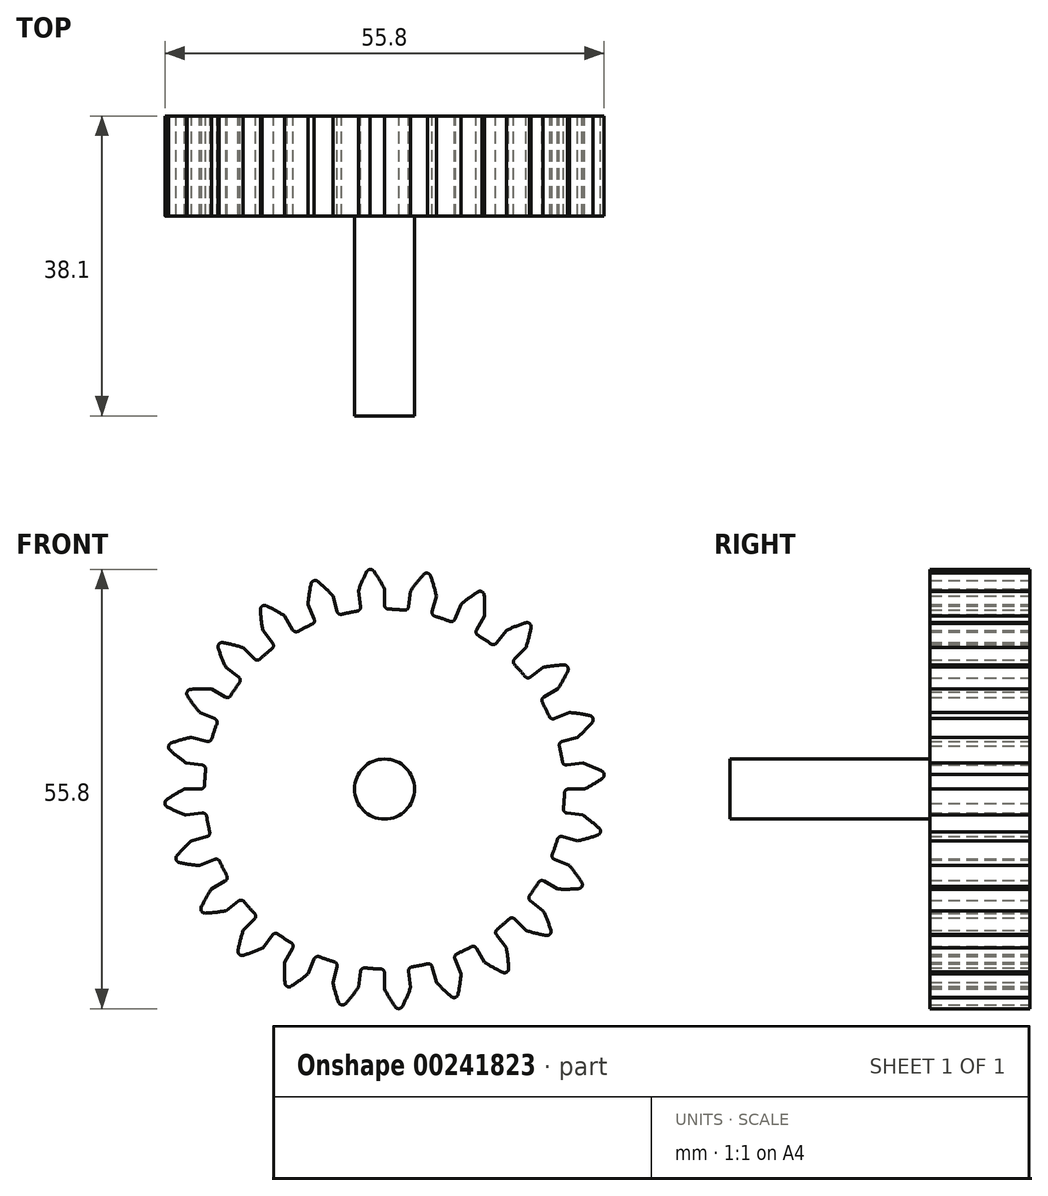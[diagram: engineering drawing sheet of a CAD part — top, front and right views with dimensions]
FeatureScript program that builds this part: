
annotation { "Feature Type Name" : "Feature", "Feature Type Description" : "" }
export const myFeature = defineFeature(function(context is Context, id is Id, definition is map)
    precondition{}
    {
        {
            var Q0;
            Q0=qCreatedBy(makeId("Front.planeOp"),FACE);
            var sketch = newSketch(context, id + "F0", { "sketchPlane" : qUnion([Q0])});
            skArc(sketch, "E0", {"start": v(-3.48, 22.6) * mm, "mid": v(1.5, -22.81) * mm, "end": v(0.5, 22.85) * mm});
            skLineSegment(sketch, "E1", {"start": v(0, 0) * mm, "end": v(-3.07, 46.82) * mm, "construction": true});
            skArc(sketch, "E2", {"start": v(0, 25.4) * mm, "mid": v(-0.64, 26.56) * mm, "end": v(-1.37, 27.68) * mm});
            skLineSegment(sketch, "E3", {"start": v(-1.78, 27.9) * mm, "end": v(-1.83, 27.9) * mm});
            skLineSegment(sketch, "E4", {"start": v(0, 25.4) * mm, "end": v(0, 23.36) * mm});
            skLineSegment(sketch, "E5.MirrorCS", {"start": v(-1.87, 27.9) * mm, "end": v(-1.83, 27.9) * mm});
            skArc(sketch, "E6.MirrorCS", {"start": v(-3.32, 25.18) * mm, "mid": v(-2.83, 26.42) * mm, "end": v(-2.26, 27.62) * mm});
            skLineSegment(sketch, "E7.MirrorCS", {"start": v(-3.32, 25.18) * mm, "end": v(-3.05, 23.16) * mm});
            skPoint(sketch, "E8.visualSharp", {"position": v(-2.13, 27.86) * mm});
            skArc(sketch, "E8.filletArc", {"start": v(-1.87, 27.9) * mm, "mid": v(-2.1, 27.8) * mm, "end": v(-2.26, 27.62) * mm});
            skPoint(sketch, "E9.visualSharp", {"position": v(0, 22.86) * mm});
            skArc(sketch, "E9.filletArc", {"start": v(0, 23.36) * mm, "mid": v(0.14, 23) * mm, "end": v(0.5, 22.85) * mm});
            skPoint(sketch, "E10.visualSharp", {"position": v(-1.52, 27.9) * mm});
            skArc(sketch, "E10.filletArc", {"start": v(-1.37, 27.68) * mm, "mid": v(-1.55, 27.84) * mm, "end": v(-1.78, 27.9) * mm});
            skPoint(sketch, "E11.visualSharp", {"position": v(-2.98, 22.66) * mm});
            skArc(sketch, "E11.filletArc", {"start": v(-3.48, 22.6) * mm, "mid": v(-3.15, 22.8) * mm, "end": v(-3.05, 23.16) * mm});
            skArc(sketch, "E12.1.0", {"start": v(-9.03, 26.46) * mm, "mid": v(-9.22, 26.31) * mm, "end": v(-9.33, 26.1) * mm});
            skLineSegment(sketch, "E12.1.1", {"start": v(-9.03, 26.46) * mm, "end": v(-8.99, 26.47) * mm});
            skLineSegment(sketch, "E12.1.2", {"start": v(-8.94, 26.49) * mm, "end": v(-8.99, 26.47) * mm});
            skArc(sketch, "E12.1.3", {"start": v(-8.49, 26.38) * mm, "mid": v(-8.7, 26.5) * mm, "end": v(-8.94, 26.49) * mm});
            skArc(sketch, "E12.1.4", {"start": v(-6.57, 24.53) * mm, "mid": v(-7.5, 25.5) * mm, "end": v(-8.49, 26.38) * mm});
            skArc(sketch, "E12.1.5", {"start": v(-9.72, 23.47) * mm, "mid": v(-9.57, 24.79) * mm, "end": v(-9.33, 26.1) * mm});
            skLineSegment(sketch, "E12.1.6", {"start": v(-6.57, 24.53) * mm, "end": v(-6.05, 22.57) * mm});
            skArc(sketch, "E12.1.7", {"start": v(-6.05, 22.57) * mm, "mid": v(-5.81, 22.26) * mm, "end": v(-5.44, 22.2) * mm});
            skArc(sketch, "E12.1.8", {"start": v(-9.2, 20.92) * mm, "mid": v(-8.94, 21.2) * mm, "end": v(-8.94, 21.58) * mm});
            skLineSegment(sketch, "E12.1.9", {"start": v(-9.72, 23.47) * mm, "end": v(-8.94, 21.58) * mm});
            skArc(sketch, "E12.2.0", {"start": v(-15.57, 23.22) * mm, "mid": v(-15.72, 23.03) * mm, "end": v(-15.77, 22.8) * mm});
            skLineSegment(sketch, "E12.2.1", {"start": v(-15.57, 23.22) * mm, "end": v(-15.53, 23.25) * mm});
            skLineSegment(sketch, "E12.2.2", {"start": v(-15.5, 23.27) * mm, "end": v(-15.53, 23.25) * mm});
            skArc(sketch, "E12.2.3", {"start": v(-15.03, 23.29) * mm, "mid": v(-15.26, 23.34) * mm, "end": v(-15.5, 23.27) * mm});
            skArc(sketch, "E12.2.4", {"start": v(-12.7, 22) * mm, "mid": v(-13.84, 22.68) * mm, "end": v(-15.03, 23.29) * mm});
            skArc(sketch, "E12.2.5", {"start": v(-15.46, 20.15) * mm, "mid": v(-15.66, 21.47) * mm, "end": v(-15.77, 22.8) * mm});
            skLineSegment(sketch, "E12.2.6", {"start": v(-12.7, 22) * mm, "end": v(-11.68, 20.23) * mm});
            skArc(sketch, "E12.2.7", {"start": v(-11.68, 20.23) * mm, "mid": v(-11.38, 20) * mm, "end": v(-11, 20.04) * mm});
            skArc(sketch, "E12.2.8", {"start": v(-14.3, 17.83) * mm, "mid": v(-14.12, 18.16) * mm, "end": v(-14.22, 18.53) * mm});
            skLineSegment(sketch, "E12.2.9", {"start": v(-15.46, 20.15) * mm, "end": v(-14.22, 18.53) * mm});
            skArc(sketch, "E12.3.0", {"start": v(-21.05, 18.4) * mm, "mid": v(-21.14, 18.18) * mm, "end": v(-21.13, 17.94) * mm});
            skLineSegment(sketch, "E12.3.1", {"start": v(-21.05, 18.4) * mm, "end": v(-21.02, 18.43) * mm});
            skLineSegment(sketch, "E12.3.2", {"start": v(-20.99, 18.47) * mm, "end": v(-21.02, 18.43) * mm});
            skArc(sketch, "E12.3.3", {"start": v(-20.54, 18.6) * mm, "mid": v(-20.78, 18.6) * mm, "end": v(-20.99, 18.47) * mm});
            skArc(sketch, "E12.3.4", {"start": v(-17.96, 17.96) * mm, "mid": v(-19.24, 18.33) * mm, "end": v(-20.54, 18.6) * mm});
            skArc(sketch, "E12.3.5", {"start": v(-20.15, 15.46) * mm, "mid": v(-20.68, 16.68) * mm, "end": v(-21.13, 17.94) * mm});
            skLineSegment(sketch, "E12.3.6", {"start": v(-17.96, 17.96) * mm, "end": v(-16.52, 16.52) * mm});
            skArc(sketch, "E12.3.7", {"start": v(-16.52, 16.52) * mm, "mid": v(-16.17, 16.37) * mm, "end": v(-15.8, 16.51) * mm});
            skArc(sketch, "E12.3.8", {"start": v(-18.43, 13.52) * mm, "mid": v(-18.34, 13.9) * mm, "end": v(-18.53, 14.22) * mm});
            skLineSegment(sketch, "E12.3.9", {"start": v(-20.15, 15.46) * mm, "end": v(-18.53, 14.22) * mm});
            skArc(sketch, "E12.4.0", {"start": v(-25.1, 12.32) * mm, "mid": v(-25.13, 12.09) * mm, "end": v(-25.05, 11.86) * mm});
            skLineSegment(sketch, "E12.4.1", {"start": v(-25.1, 12.32) * mm, "end": v(-25.08, 12.37) * mm});
            skLineSegment(sketch, "E12.4.2", {"start": v(-25.05, 12.4) * mm, "end": v(-25.08, 12.37) * mm});
            skArc(sketch, "E12.4.3", {"start": v(-24.66, 12.66) * mm, "mid": v(-24.89, 12.58) * mm, "end": v(-25.05, 12.4) * mm});
            skArc(sketch, "E12.4.4", {"start": v(-22, 12.7) * mm, "mid": v(-23.33, 12.72) * mm, "end": v(-24.66, 12.66) * mm});
            skArc(sketch, "E12.4.5", {"start": v(-23.47, 9.72) * mm, "mid": v(-24.3, 10.76) * mm, "end": v(-25.05, 11.86) * mm});
            skLineSegment(sketch, "E12.4.6", {"start": v(-22, 12.7) * mm, "end": v(-20.23, 11.68) * mm});
            skArc(sketch, "E12.4.7", {"start": v(-20.23, 11.68) * mm, "mid": v(-19.85, 11.63) * mm, "end": v(-19.54, 11.86) * mm});
            skArc(sketch, "E12.4.8", {"start": v(-21.3, 8.29) * mm, "mid": v(-21.31, 8.67) * mm, "end": v(-21.58, 8.94) * mm});
            skLineSegment(sketch, "E12.4.9", {"start": v(-23.47, 9.72) * mm, "end": v(-21.58, 8.94) * mm});
            skArc(sketch, "E12.5.0", {"start": v(-27.43, 5.41) * mm, "mid": v(-27.4, 5.17) * mm, "end": v(-27.27, 4.97) * mm});
            skLineSegment(sketch, "E12.5.1", {"start": v(-27.43, 5.41) * mm, "end": v(-27.42, 5.45) * mm});
            skLineSegment(sketch, "E12.5.2", {"start": v(-27.4, 5.5) * mm, "end": v(-27.42, 5.45) * mm});
            skArc(sketch, "E12.5.3", {"start": v(-27.1, 5.84) * mm, "mid": v(-27.3, 5.7) * mm, "end": v(-27.4, 5.5) * mm});
            skArc(sketch, "E12.5.4", {"start": v(-24.53, 6.57) * mm, "mid": v(-25.83, 6.25) * mm, "end": v(-27.1, 5.84) * mm});
            skArc(sketch, "E12.5.5", {"start": v(-25.18, 3.32) * mm, "mid": v(-26.25, 4.1) * mm, "end": v(-27.27, 4.97) * mm});
            skLineSegment(sketch, "E12.5.6", {"start": v(-24.53, 6.57) * mm, "end": v(-22.57, 6.05) * mm});
            skArc(sketch, "E12.5.7", {"start": v(-22.57, 6.05) * mm, "mid": v(-22.19, 6.1) * mm, "end": v(-21.95, 6.4) * mm});
            skArc(sketch, "E12.5.8", {"start": v(-22.72, 2.5) * mm, "mid": v(-22.83, 2.86) * mm, "end": v(-23.16, 3.05) * mm});
            skLineSegment(sketch, "E12.5.9", {"start": v(-25.18, 3.32) * mm, "end": v(-23.16, 3.05) * mm});
            skArc(sketch, "E12.6.0", {"start": v(-27.9, -1.87) * mm, "mid": v(-27.8, -2.1) * mm, "end": v(-27.62, -2.26) * mm});
            skLineSegment(sketch, "E12.6.1", {"start": v(-27.9, -1.87) * mm, "end": v(-27.9, -1.83) * mm});
            skLineSegment(sketch, "E12.6.2", {"start": v(-27.9, -1.78) * mm, "end": v(-27.9, -1.83) * mm});
            skArc(sketch, "E12.6.3", {"start": v(-27.68, -1.37) * mm, "mid": v(-27.84, -1.55) * mm, "end": v(-27.9, -1.78) * mm});
            skArc(sketch, "E12.6.4", {"start": v(-25.4, 0) * mm, "mid": v(-26.56, -0.64) * mm, "end": v(-27.68, -1.37) * mm});
            skArc(sketch, "E12.6.5", {"start": v(-25.18, -3.32) * mm, "mid": v(-26.42, -2.83) * mm, "end": v(-27.62, -2.26) * mm});
            skLineSegment(sketch, "E12.6.6", {"start": v(-25.4, 0) * mm, "end": v(-23.36, 0) * mm});
            skArc(sketch, "E12.6.7", {"start": v(-23.36, 0) * mm, "mid": v(-23, 0.14) * mm, "end": v(-22.85, 0.5) * mm});
            skArc(sketch, "E12.6.8", {"start": v(-22.6, -3.48) * mm, "mid": v(-22.8, -3.15) * mm, "end": v(-23.16, -3.05) * mm});
            skLineSegment(sketch, "E12.6.9", {"start": v(-25.18, -3.32) * mm, "end": v(-23.16, -3.05) * mm});
            skArc(sketch, "E12.7.0", {"start": v(-26.46, -9.03) * mm, "mid": v(-26.31, -9.22) * mm, "end": v(-26.1, -9.33) * mm});
            skLineSegment(sketch, "E12.7.1", {"start": v(-26.46, -9.03) * mm, "end": v(-26.47, -8.99) * mm});
            skLineSegment(sketch, "E12.7.2", {"start": v(-26.49, -8.94) * mm, "end": v(-26.47, -8.99) * mm});
            skArc(sketch, "E12.7.3", {"start": v(-26.38, -8.49) * mm, "mid": v(-26.5, -8.7) * mm, "end": v(-26.49, -8.94) * mm});
            skArc(sketch, "E12.7.4", {"start": v(-24.53, -6.57) * mm, "mid": v(-25.5, -7.5) * mm, "end": v(-26.38, -8.49) * mm});
            skArc(sketch, "E12.7.5", {"start": v(-23.47, -9.72) * mm, "mid": v(-24.79, -9.57) * mm, "end": v(-26.1, -9.33) * mm});
            skLineSegment(sketch, "E12.7.6", {"start": v(-24.53, -6.57) * mm, "end": v(-22.57, -6.05) * mm});
            skArc(sketch, "E12.7.7", {"start": v(-22.57, -6.05) * mm, "mid": v(-22.26, -5.81) * mm, "end": v(-22.2, -5.44) * mm});
            skArc(sketch, "E12.7.8", {"start": v(-20.92, -9.2) * mm, "mid": v(-21.2, -8.94) * mm, "end": v(-21.58, -8.94) * mm});
            skLineSegment(sketch, "E12.7.9", {"start": v(-23.47, -9.72) * mm, "end": v(-21.58, -8.94) * mm});
            skArc(sketch, "E12.8.0", {"start": v(-23.22, -15.57) * mm, "mid": v(-23.03, -15.72) * mm, "end": v(-22.8, -15.77) * mm});
            skLineSegment(sketch, "E12.8.1", {"start": v(-23.22, -15.57) * mm, "end": v(-23.25, -15.53) * mm});
            skLineSegment(sketch, "E12.8.2", {"start": v(-23.27, -15.5) * mm, "end": v(-23.25, -15.53) * mm});
            skArc(sketch, "E12.8.3", {"start": v(-23.29, -15.03) * mm, "mid": v(-23.34, -15.26) * mm, "end": v(-23.27, -15.5) * mm});
            skArc(sketch, "E12.8.4", {"start": v(-22, -12.7) * mm, "mid": v(-22.68, -13.84) * mm, "end": v(-23.29, -15.03) * mm});
            skArc(sketch, "E12.8.5", {"start": v(-20.15, -15.46) * mm, "mid": v(-21.47, -15.66) * mm, "end": v(-22.8, -15.77) * mm});
            skLineSegment(sketch, "E12.8.6", {"start": v(-22, -12.7) * mm, "end": v(-20.23, -11.68) * mm});
            skArc(sketch, "E12.8.7", {"start": v(-20.23, -11.68) * mm, "mid": v(-20, -11.38) * mm, "end": v(-20.04, -11) * mm});
            skArc(sketch, "E12.8.8", {"start": v(-17.83, -14.3) * mm, "mid": v(-18.16, -14.12) * mm, "end": v(-18.53, -14.22) * mm});
            skLineSegment(sketch, "E12.8.9", {"start": v(-20.15, -15.46) * mm, "end": v(-18.53, -14.22) * mm});
            skArc(sketch, "E12.9.0", {"start": v(-18.4, -21.05) * mm, "mid": v(-18.18, -21.14) * mm, "end": v(-17.94, -21.13) * mm});
            skLineSegment(sketch, "E12.9.1", {"start": v(-18.4, -21.05) * mm, "end": v(-18.43, -21.02) * mm});
            skLineSegment(sketch, "E12.9.2", {"start": v(-18.47, -20.99) * mm, "end": v(-18.43, -21.02) * mm});
            skArc(sketch, "E12.9.3", {"start": v(-18.6, -20.54) * mm, "mid": v(-18.6, -20.78) * mm, "end": v(-18.47, -20.99) * mm});
            skArc(sketch, "E12.9.4", {"start": v(-17.96, -17.96) * mm, "mid": v(-18.33, -19.24) * mm, "end": v(-18.6, -20.54) * mm});
            skArc(sketch, "E12.9.5", {"start": v(-15.46, -20.15) * mm, "mid": v(-16.68, -20.68) * mm, "end": v(-17.94, -21.13) * mm});
            skLineSegment(sketch, "E12.9.6", {"start": v(-17.96, -17.96) * mm, "end": v(-16.52, -16.52) * mm});
            skArc(sketch, "E12.9.7", {"start": v(-16.52, -16.52) * mm, "mid": v(-16.37, -16.17) * mm, "end": v(-16.51, -15.8) * mm});
            skArc(sketch, "E12.9.8", {"start": v(-13.52, -18.43) * mm, "mid": v(-13.9, -18.34) * mm, "end": v(-14.22, -18.53) * mm});
            skLineSegment(sketch, "E12.9.9", {"start": v(-15.46, -20.15) * mm, "end": v(-14.22, -18.53) * mm});
            skArc(sketch, "E12.10.0", {"start": v(-12.32, -25.1) * mm, "mid": v(-12.09, -25.13) * mm, "end": v(-11.86, -25.05) * mm});
            skLineSegment(sketch, "E12.10.1", {"start": v(-12.32, -25.1) * mm, "end": v(-12.37, -25.08) * mm});
            skLineSegment(sketch, "E12.10.2", {"start": v(-12.4, -25.05) * mm, "end": v(-12.37, -25.08) * mm});
            skArc(sketch, "E12.10.3", {"start": v(-12.66, -24.66) * mm, "mid": v(-12.58, -24.89) * mm, "end": v(-12.4, -25.05) * mm});
            skArc(sketch, "E12.10.4", {"start": v(-12.7, -22) * mm, "mid": v(-12.72, -23.33) * mm, "end": v(-12.66, -24.66) * mm});
            skArc(sketch, "E12.10.5", {"start": v(-9.72, -23.47) * mm, "mid": v(-10.76, -24.3) * mm, "end": v(-11.86, -25.05) * mm});
            skLineSegment(sketch, "E12.10.6", {"start": v(-12.7, -22) * mm, "end": v(-11.68, -20.23) * mm});
            skArc(sketch, "E12.10.7", {"start": v(-11.68, -20.23) * mm, "mid": v(-11.63, -19.85) * mm, "end": v(-11.86, -19.54) * mm});
            skArc(sketch, "E12.10.8", {"start": v(-8.29, -21.3) * mm, "mid": v(-8.67, -21.31) * mm, "end": v(-8.94, -21.58) * mm});
            skLineSegment(sketch, "E12.10.9", {"start": v(-9.72, -23.47) * mm, "end": v(-8.94, -21.58) * mm});
            skArc(sketch, "E12.11.0", {"start": v(-5.41, -27.43) * mm, "mid": v(-5.17, -27.4) * mm, "end": v(-4.97, -27.27) * mm});
            skLineSegment(sketch, "E12.11.1", {"start": v(-5.41, -27.43) * mm, "end": v(-5.45, -27.42) * mm});
            skLineSegment(sketch, "E12.11.2", {"start": v(-5.5, -27.4) * mm, "end": v(-5.45, -27.42) * mm});
            skArc(sketch, "E12.11.3", {"start": v(-5.84, -27.1) * mm, "mid": v(-5.7, -27.3) * mm, "end": v(-5.5, -27.4) * mm});
            skArc(sketch, "E12.11.4", {"start": v(-6.57, -24.53) * mm, "mid": v(-6.25, -25.83) * mm, "end": v(-5.84, -27.1) * mm});
            skArc(sketch, "E12.11.5", {"start": v(-3.32, -25.18) * mm, "mid": v(-4.1, -26.25) * mm, "end": v(-4.97, -27.27) * mm});
            skLineSegment(sketch, "E12.11.6", {"start": v(-6.57, -24.53) * mm, "end": v(-6.05, -22.57) * mm});
            skArc(sketch, "E12.11.7", {"start": v(-6.05, -22.57) * mm, "mid": v(-6.1, -22.19) * mm, "end": v(-6.4, -21.95) * mm});
            skArc(sketch, "E12.11.8", {"start": v(-2.5, -22.72) * mm, "mid": v(-2.86, -22.83) * mm, "end": v(-3.05, -23.16) * mm});
            skLineSegment(sketch, "E12.11.9", {"start": v(-3.32, -25.18) * mm, "end": v(-3.05, -23.16) * mm});
            skArc(sketch, "E12.12.0", {"start": v(1.87, -27.9) * mm, "mid": v(2.1, -27.8) * mm, "end": v(2.26, -27.62) * mm});
            skLineSegment(sketch, "E12.12.1", {"start": v(1.87, -27.9) * mm, "end": v(1.83, -27.9) * mm});
            skLineSegment(sketch, "E12.12.2", {"start": v(1.78, -27.9) * mm, "end": v(1.83, -27.9) * mm});
            skArc(sketch, "E12.12.3", {"start": v(1.37, -27.68) * mm, "mid": v(1.55, -27.84) * mm, "end": v(1.78, -27.9) * mm});
            skArc(sketch, "E12.12.4", {"start": v(0, -25.4) * mm, "mid": v(0.64, -26.56) * mm, "end": v(1.37, -27.68) * mm});
            skArc(sketch, "E12.12.5", {"start": v(3.32, -25.18) * mm, "mid": v(2.83, -26.42) * mm, "end": v(2.26, -27.62) * mm});
            skLineSegment(sketch, "E12.12.6", {"start": v(0, -25.4) * mm, "end": v(0, -23.36) * mm});
            skArc(sketch, "E12.12.7", {"start": v(0, -23.36) * mm, "mid": v(-0.14, -23) * mm, "end": v(-0.5, -22.85) * mm});
            skArc(sketch, "E12.12.8", {"start": v(3.48, -22.6) * mm, "mid": v(3.15, -22.8) * mm, "end": v(3.05, -23.16) * mm});
            skLineSegment(sketch, "E12.12.9", {"start": v(3.32, -25.18) * mm, "end": v(3.05, -23.16) * mm});
            skArc(sketch, "E12.13.0", {"start": v(9.03, -26.46) * mm, "mid": v(9.22, -26.31) * mm, "end": v(9.33, -26.1) * mm});
            skLineSegment(sketch, "E12.13.1", {"start": v(9.03, -26.46) * mm, "end": v(8.99, -26.47) * mm});
            skLineSegment(sketch, "E12.13.2", {"start": v(8.94, -26.49) * mm, "end": v(8.99, -26.47) * mm});
            skArc(sketch, "E12.13.3", {"start": v(8.49, -26.38) * mm, "mid": v(8.7, -26.5) * mm, "end": v(8.94, -26.49) * mm});
            skArc(sketch, "E12.13.4", {"start": v(6.57, -24.53) * mm, "mid": v(7.5, -25.5) * mm, "end": v(8.49, -26.38) * mm});
            skArc(sketch, "E12.13.5", {"start": v(9.72, -23.47) * mm, "mid": v(9.57, -24.79) * mm, "end": v(9.33, -26.1) * mm});
            skLineSegment(sketch, "E12.13.6", {"start": v(6.57, -24.53) * mm, "end": v(6.05, -22.57) * mm});
            skArc(sketch, "E12.13.7", {"start": v(6.05, -22.57) * mm, "mid": v(5.81, -22.26) * mm, "end": v(5.44, -22.2) * mm});
            skArc(sketch, "E12.13.8", {"start": v(9.2, -20.92) * mm, "mid": v(8.94, -21.2) * mm, "end": v(8.94, -21.58) * mm});
            skLineSegment(sketch, "E12.13.9", {"start": v(9.72, -23.47) * mm, "end": v(8.94, -21.58) * mm});
            skArc(sketch, "E12.14.0", {"start": v(15.57, -23.22) * mm, "mid": v(15.72, -23.03) * mm, "end": v(15.77, -22.8) * mm});
            skLineSegment(sketch, "E12.14.1", {"start": v(15.57, -23.22) * mm, "end": v(15.53, -23.25) * mm});
            skLineSegment(sketch, "E12.14.2", {"start": v(15.5, -23.27) * mm, "end": v(15.53, -23.25) * mm});
            skArc(sketch, "E12.14.3", {"start": v(15.03, -23.29) * mm, "mid": v(15.26, -23.34) * mm, "end": v(15.5, -23.27) * mm});
            skArc(sketch, "E12.14.4", {"start": v(12.7, -22) * mm, "mid": v(13.84, -22.68) * mm, "end": v(15.03, -23.29) * mm});
            skArc(sketch, "E12.14.5", {"start": v(15.46, -20.15) * mm, "mid": v(15.66, -21.47) * mm, "end": v(15.77, -22.8) * mm});
            skLineSegment(sketch, "E12.14.6", {"start": v(12.7, -22) * mm, "end": v(11.68, -20.23) * mm});
            skArc(sketch, "E12.14.7", {"start": v(11.68, -20.23) * mm, "mid": v(11.38, -20) * mm, "end": v(11, -20.04) * mm});
            skArc(sketch, "E12.14.8", {"start": v(14.3, -17.83) * mm, "mid": v(14.12, -18.16) * mm, "end": v(14.22, -18.53) * mm});
            skLineSegment(sketch, "E12.14.9", {"start": v(15.46, -20.15) * mm, "end": v(14.22, -18.53) * mm});
            skArc(sketch, "E12.15.0", {"start": v(21.05, -18.4) * mm, "mid": v(21.14, -18.18) * mm, "end": v(21.13, -17.94) * mm});
            skLineSegment(sketch, "E12.15.1", {"start": v(21.05, -18.4) * mm, "end": v(21.02, -18.43) * mm});
            skLineSegment(sketch, "E12.15.2", {"start": v(20.99, -18.47) * mm, "end": v(21.02, -18.43) * mm});
            skArc(sketch, "E12.15.3", {"start": v(20.54, -18.6) * mm, "mid": v(20.78, -18.6) * mm, "end": v(20.99, -18.47) * mm});
            skArc(sketch, "E12.15.4", {"start": v(17.96, -17.96) * mm, "mid": v(19.24, -18.33) * mm, "end": v(20.54, -18.6) * mm});
            skArc(sketch, "E12.15.5", {"start": v(20.15, -15.46) * mm, "mid": v(20.68, -16.68) * mm, "end": v(21.13, -17.94) * mm});
            skLineSegment(sketch, "E12.15.6", {"start": v(17.96, -17.96) * mm, "end": v(16.52, -16.52) * mm});
            skArc(sketch, "E12.15.7", {"start": v(16.52, -16.52) * mm, "mid": v(16.17, -16.37) * mm, "end": v(15.8, -16.51) * mm});
            skArc(sketch, "E12.15.8", {"start": v(18.43, -13.52) * mm, "mid": v(18.34, -13.9) * mm, "end": v(18.53, -14.22) * mm});
            skLineSegment(sketch, "E12.15.9", {"start": v(20.15, -15.46) * mm, "end": v(18.53, -14.22) * mm});
            skArc(sketch, "E12.16.0", {"start": v(25.1, -12.32) * mm, "mid": v(25.13, -12.09) * mm, "end": v(25.05, -11.86) * mm});
            skLineSegment(sketch, "E12.16.1", {"start": v(25.1, -12.32) * mm, "end": v(25.08, -12.37) * mm});
            skLineSegment(sketch, "E12.16.2", {"start": v(25.05, -12.4) * mm, "end": v(25.08, -12.37) * mm});
            skArc(sketch, "E12.16.3", {"start": v(24.66, -12.66) * mm, "mid": v(24.89, -12.58) * mm, "end": v(25.05, -12.4) * mm});
            skArc(sketch, "E12.16.4", {"start": v(22, -12.7) * mm, "mid": v(23.33, -12.72) * mm, "end": v(24.66, -12.66) * mm});
            skArc(sketch, "E12.16.5", {"start": v(23.47, -9.72) * mm, "mid": v(24.3, -10.76) * mm, "end": v(25.05, -11.86) * mm});
            skLineSegment(sketch, "E12.16.6", {"start": v(22, -12.7) * mm, "end": v(20.23, -11.68) * mm});
            skArc(sketch, "E12.16.7", {"start": v(20.23, -11.68) * mm, "mid": v(19.85, -11.63) * mm, "end": v(19.54, -11.86) * mm});
            skArc(sketch, "E12.16.8", {"start": v(21.3, -8.29) * mm, "mid": v(21.31, -8.67) * mm, "end": v(21.58, -8.94) * mm});
            skLineSegment(sketch, "E12.16.9", {"start": v(23.47, -9.72) * mm, "end": v(21.58, -8.94) * mm});
            skArc(sketch, "E12.17.0", {"start": v(27.43, -5.41) * mm, "mid": v(27.4, -5.17) * mm, "end": v(27.27, -4.97) * mm});
            skLineSegment(sketch, "E12.17.1", {"start": v(27.43, -5.41) * mm, "end": v(27.42, -5.45) * mm});
            skLineSegment(sketch, "E12.17.2", {"start": v(27.4, -5.5) * mm, "end": v(27.42, -5.45) * mm});
            skArc(sketch, "E12.17.3", {"start": v(27.1, -5.84) * mm, "mid": v(27.3, -5.7) * mm, "end": v(27.4, -5.5) * mm});
            skArc(sketch, "E12.17.4", {"start": v(24.53, -6.57) * mm, "mid": v(25.83, -6.25) * mm, "end": v(27.1, -5.84) * mm});
            skArc(sketch, "E12.17.5", {"start": v(25.18, -3.32) * mm, "mid": v(26.25, -4.1) * mm, "end": v(27.27, -4.97) * mm});
            skLineSegment(sketch, "E12.17.6", {"start": v(24.53, -6.57) * mm, "end": v(22.57, -6.05) * mm});
            skArc(sketch, "E12.17.7", {"start": v(22.57, -6.05) * mm, "mid": v(22.19, -6.1) * mm, "end": v(21.95, -6.4) * mm});
            skArc(sketch, "E12.17.8", {"start": v(22.72, -2.5) * mm, "mid": v(22.83, -2.86) * mm, "end": v(23.16, -3.05) * mm});
            skLineSegment(sketch, "E12.17.9", {"start": v(25.18, -3.32) * mm, "end": v(23.16, -3.05) * mm});
            skArc(sketch, "E12.18.0", {"start": v(27.9, 1.87) * mm, "mid": v(27.8, 2.1) * mm, "end": v(27.62, 2.26) * mm});
            skLineSegment(sketch, "E12.18.1", {"start": v(27.9, 1.87) * mm, "end": v(27.9, 1.83) * mm});
            skLineSegment(sketch, "E12.18.2", {"start": v(27.9, 1.78) * mm, "end": v(27.9, 1.83) * mm});
            skArc(sketch, "E12.18.3", {"start": v(27.68, 1.37) * mm, "mid": v(27.84, 1.55) * mm, "end": v(27.9, 1.78) * mm});
            skArc(sketch, "E12.18.4", {"start": v(25.4, 0) * mm, "mid": v(26.56, 0.64) * mm, "end": v(27.68, 1.37) * mm});
            skArc(sketch, "E12.18.5", {"start": v(25.18, 3.32) * mm, "mid": v(26.42, 2.83) * mm, "end": v(27.62, 2.26) * mm});
            skLineSegment(sketch, "E12.18.6", {"start": v(25.4, 0) * mm, "end": v(23.36, 0) * mm});
            skArc(sketch, "E12.18.7", {"start": v(23.36, 0) * mm, "mid": v(23, -0.14) * mm, "end": v(22.85, -0.5) * mm});
            skArc(sketch, "E12.18.8", {"start": v(22.6, 3.48) * mm, "mid": v(22.8, 3.15) * mm, "end": v(23.16, 3.05) * mm});
            skLineSegment(sketch, "E12.18.9", {"start": v(25.18, 3.32) * mm, "end": v(23.16, 3.05) * mm});
            skArc(sketch, "E12.19.0", {"start": v(26.46, 9.03) * mm, "mid": v(26.31, 9.22) * mm, "end": v(26.1, 9.33) * mm});
            skLineSegment(sketch, "E12.19.1", {"start": v(26.46, 9.03) * mm, "end": v(26.47, 8.99) * mm});
            skLineSegment(sketch, "E12.19.2", {"start": v(26.49, 8.94) * mm, "end": v(26.47, 8.99) * mm});
            skArc(sketch, "E12.19.3", {"start": v(26.38, 8.49) * mm, "mid": v(26.5, 8.7) * mm, "end": v(26.49, 8.94) * mm});
            skArc(sketch, "E12.19.4", {"start": v(24.53, 6.57) * mm, "mid": v(25.5, 7.5) * mm, "end": v(26.38, 8.49) * mm});
            skArc(sketch, "E12.19.5", {"start": v(23.47, 9.72) * mm, "mid": v(24.79, 9.57) * mm, "end": v(26.1, 9.33) * mm});
            skLineSegment(sketch, "E12.19.6", {"start": v(24.53, 6.57) * mm, "end": v(22.57, 6.05) * mm});
            skArc(sketch, "E12.19.7", {"start": v(22.57, 6.05) * mm, "mid": v(22.26, 5.81) * mm, "end": v(22.2, 5.44) * mm});
            skArc(sketch, "E12.19.8", {"start": v(20.92, 9.2) * mm, "mid": v(21.2, 8.94) * mm, "end": v(21.58, 8.94) * mm});
            skLineSegment(sketch, "E12.19.9", {"start": v(23.47, 9.72) * mm, "end": v(21.58, 8.94) * mm});
            skArc(sketch, "E12.20.0", {"start": v(23.22, 15.57) * mm, "mid": v(23.03, 15.72) * mm, "end": v(22.8, 15.77) * mm});
            skLineSegment(sketch, "E12.20.1", {"start": v(23.22, 15.57) * mm, "end": v(23.25, 15.53) * mm});
            skLineSegment(sketch, "E12.20.2", {"start": v(23.27, 15.5) * mm, "end": v(23.25, 15.53) * mm});
            skArc(sketch, "E12.20.3", {"start": v(23.29, 15.03) * mm, "mid": v(23.34, 15.26) * mm, "end": v(23.27, 15.5) * mm});
            skArc(sketch, "E12.20.4", {"start": v(22, 12.7) * mm, "mid": v(22.68, 13.84) * mm, "end": v(23.29, 15.03) * mm});
            skArc(sketch, "E12.20.5", {"start": v(20.15, 15.46) * mm, "mid": v(21.47, 15.66) * mm, "end": v(22.8, 15.77) * mm});
            skLineSegment(sketch, "E12.20.6", {"start": v(22, 12.7) * mm, "end": v(20.23, 11.68) * mm});
            skArc(sketch, "E12.20.7", {"start": v(20.23, 11.68) * mm, "mid": v(20, 11.38) * mm, "end": v(20.04, 11) * mm});
            skArc(sketch, "E12.20.8", {"start": v(17.83, 14.3) * mm, "mid": v(18.16, 14.12) * mm, "end": v(18.53, 14.22) * mm});
            skLineSegment(sketch, "E12.20.9", {"start": v(20.15, 15.46) * mm, "end": v(18.53, 14.22) * mm});
            skArc(sketch, "E12.21.0", {"start": v(18.4, 21.05) * mm, "mid": v(18.18, 21.14) * mm, "end": v(17.94, 21.13) * mm});
            skLineSegment(sketch, "E12.21.1", {"start": v(18.4, 21.05) * mm, "end": v(18.43, 21.02) * mm});
            skLineSegment(sketch, "E12.21.2", {"start": v(18.47, 20.99) * mm, "end": v(18.43, 21.02) * mm});
            skArc(sketch, "E12.21.3", {"start": v(18.6, 20.54) * mm, "mid": v(18.6, 20.78) * mm, "end": v(18.47, 20.99) * mm});
            skArc(sketch, "E12.21.4", {"start": v(17.96, 17.96) * mm, "mid": v(18.33, 19.24) * mm, "end": v(18.6, 20.54) * mm});
            skArc(sketch, "E12.21.5", {"start": v(15.46, 20.15) * mm, "mid": v(16.68, 20.68) * mm, "end": v(17.94, 21.13) * mm});
            skLineSegment(sketch, "E12.21.6", {"start": v(17.96, 17.96) * mm, "end": v(16.52, 16.52) * mm});
            skArc(sketch, "E12.21.7", {"start": v(16.52, 16.52) * mm, "mid": v(16.37, 16.17) * mm, "end": v(16.51, 15.8) * mm});
            skArc(sketch, "E12.21.8", {"start": v(13.52, 18.43) * mm, "mid": v(13.9, 18.34) * mm, "end": v(14.22, 18.53) * mm});
            skLineSegment(sketch, "E12.21.9", {"start": v(15.46, 20.15) * mm, "end": v(14.22, 18.53) * mm});
            skArc(sketch, "E12.22.0", {"start": v(12.32, 25.1) * mm, "mid": v(12.09, 25.13) * mm, "end": v(11.86, 25.05) * mm});
            skLineSegment(sketch, "E12.22.1", {"start": v(12.32, 25.1) * mm, "end": v(12.37, 25.08) * mm});
            skLineSegment(sketch, "E12.22.2", {"start": v(12.4, 25.05) * mm, "end": v(12.37, 25.08) * mm});
            skArc(sketch, "E12.22.3", {"start": v(12.66, 24.66) * mm, "mid": v(12.58, 24.89) * mm, "end": v(12.4, 25.05) * mm});
            skArc(sketch, "E12.22.4", {"start": v(12.7, 22) * mm, "mid": v(12.72, 23.33) * mm, "end": v(12.66, 24.66) * mm});
            skArc(sketch, "E12.22.5", {"start": v(9.72, 23.47) * mm, "mid": v(10.76, 24.3) * mm, "end": v(11.86, 25.05) * mm});
            skLineSegment(sketch, "E12.22.6", {"start": v(12.7, 22) * mm, "end": v(11.68, 20.23) * mm});
            skArc(sketch, "E12.22.7", {"start": v(11.68, 20.23) * mm, "mid": v(11.63, 19.85) * mm, "end": v(11.86, 19.54) * mm});
            skArc(sketch, "E12.22.8", {"start": v(8.29, 21.3) * mm, "mid": v(8.67, 21.31) * mm, "end": v(8.94, 21.58) * mm});
            skLineSegment(sketch, "E12.22.9", {"start": v(9.72, 23.47) * mm, "end": v(8.94, 21.58) * mm});
            skArc(sketch, "E12.23.0", {"start": v(5.41, 27.43) * mm, "mid": v(5.17, 27.4) * mm, "end": v(4.97, 27.27) * mm});
            skLineSegment(sketch, "E12.23.1", {"start": v(5.41, 27.43) * mm, "end": v(5.45, 27.42) * mm});
            skLineSegment(sketch, "E12.23.2", {"start": v(5.5, 27.4) * mm, "end": v(5.45, 27.42) * mm});
            skArc(sketch, "E12.23.3", {"start": v(5.84, 27.1) * mm, "mid": v(5.7, 27.3) * mm, "end": v(5.5, 27.4) * mm});
            skArc(sketch, "E12.23.4", {"start": v(6.57, 24.53) * mm, "mid": v(6.25, 25.83) * mm, "end": v(5.84, 27.1) * mm});
            skArc(sketch, "E12.23.5", {"start": v(3.32, 25.18) * mm, "mid": v(4.1, 26.25) * mm, "end": v(4.97, 27.27) * mm});
            skLineSegment(sketch, "E12.23.6", {"start": v(6.57, 24.53) * mm, "end": v(6.05, 22.57) * mm});
            skArc(sketch, "E12.23.7", {"start": v(6.05, 22.57) * mm, "mid": v(6.1, 22.19) * mm, "end": v(6.4, 21.95) * mm});
            skArc(sketch, "E12.23.8", {"start": v(2.5, 22.72) * mm, "mid": v(2.86, 22.83) * mm, "end": v(3.05, 23.16) * mm});
            skLineSegment(sketch, "E12.23.9", {"start": v(3.32, 25.18) * mm, "end": v(3.05, 23.16) * mm});
            skSolve(sketch);
        }
        {
            var Q0;
            Q0 = qSketchRegion(id + "F0", true);
            extrude(context, id + "F1", {"entities" : qUnion([Q0]), "depth" : 12.7 * mm});
        }
        {
            var Q0;
            Q0=makeQuery(id+"F1.opExtrude","CAP_FACE",FACE,{"disambiguationData":[OSD([sQuery(id+"F0.wireOp",EDGE,"E0"),sQuery(id+"F0.wireOp",EDGE,"E2"),sQuery(id+"F0.wireOp",EDGE,"E3"),sQuery(id+"F0.wireOp",EDGE,"E4"),sQuery(id+"F0.wireOp",EDGE,"E5.MirrorCS"),sQuery(id+"F0.wireOp",EDGE,"E6.MirrorCS"),sQuery(id+"F0.wireOp",EDGE,"E7.MirrorCS"),sQuery(id+"F0.wireOp",EDGE,"E8.filletArc"),sQuery(id+"F0.wireOp",EDGE,"E9.filletArc"),sQuery(id+"F0.wireOp",EDGE,"E10.filletArc"),sQuery(id+"F0.wireOp",EDGE,"E11.filletArc"),sQuery(id+"F0.wireOp",EDGE,"E12.1.0"),sQuery(id+"F0.wireOp",EDGE,"E12.1.1"),sQuery(id+"F0.wireOp",EDGE,"E12.1.2"),sQuery(id+"F0.wireOp",EDGE,"E12.1.3"),sQuery(id+"F0.wireOp",EDGE,"E12.1.4"),sQuery(id+"F0.wireOp",EDGE,"E12.1.5"),sQuery(id+"F0.wireOp",EDGE,"E12.1.6"),sQuery(id+"F0.wireOp",EDGE,"E12.1.7"),sQuery(id+"F0.wireOp",EDGE,"E12.1.8"),sQuery(id+"F0.wireOp",EDGE,"E12.1.9"),sQuery(id+"F0.wireOp",EDGE,"E12.2.0"),sQuery(id+"F0.wireOp",EDGE,"E12.2.1"),sQuery(id+"F0.wireOp",EDGE,"E12.2.2"),sQuery(id+"F0.wireOp",EDGE,"E12.2.3"),sQuery(id+"F0.wireOp",EDGE,"E12.2.4"),sQuery(id+"F0.wireOp",EDGE,"E12.2.5"),sQuery(id+"F0.wireOp",EDGE,"E12.2.6"),sQuery(id+"F0.wireOp",EDGE,"E12.2.7"),sQuery(id+"F0.wireOp",EDGE,"E12.2.8"),sQuery(id+"F0.wireOp",EDGE,"E12.2.9"),sQuery(id+"F0.wireOp",EDGE,"E12.3.0"),sQuery(id+"F0.wireOp",EDGE,"E12.3.1"),sQuery(id+"F0.wireOp",EDGE,"E12.3.2"),sQuery(id+"F0.wireOp",EDGE,"E12.3.3"),sQuery(id+"F0.wireOp",EDGE,"E12.3.4"),sQuery(id+"F0.wireOp",EDGE,"E12.3.5"),sQuery(id+"F0.wireOp",EDGE,"E12.3.6"),sQuery(id+"F0.wireOp",EDGE,"E12.3.7"),sQuery(id+"F0.wireOp",EDGE,"E12.3.8"),sQuery(id+"F0.wireOp",EDGE,"E12.3.9"),sQuery(id+"F0.wireOp",EDGE,"E12.4.0"),sQuery(id+"F0.wireOp",EDGE,"E12.4.1"),sQuery(id+"F0.wireOp",EDGE,"E12.4.2"),sQuery(id+"F0.wireOp",EDGE,"E12.4.3"),sQuery(id+"F0.wireOp",EDGE,"E12.4.4"),sQuery(id+"F0.wireOp",EDGE,"E12.4.5"),sQuery(id+"F0.wireOp",EDGE,"E12.4.6"),sQuery(id+"F0.wireOp",EDGE,"E12.4.7"),sQuery(id+"F0.wireOp",EDGE,"E12.4.8"),sQuery(id+"F0.wireOp",EDGE,"E12.4.9"),sQuery(id+"F0.wireOp",EDGE,"E12.5.0"),sQuery(id+"F0.wireOp",EDGE,"E12.5.1"),sQuery(id+"F0.wireOp",EDGE,"E12.5.2"),sQuery(id+"F0.wireOp",EDGE,"E12.5.3"),sQuery(id+"F0.wireOp",EDGE,"E12.5.4"),sQuery(id+"F0.wireOp",EDGE,"E12.5.5"),sQuery(id+"F0.wireOp",EDGE,"E12.5.6"),sQuery(id+"F0.wireOp",EDGE,"E12.5.7"),sQuery(id+"F0.wireOp",EDGE,"E12.5.8"),sQuery(id+"F0.wireOp",EDGE,"E12.5.9"),sQuery(id+"F0.wireOp",EDGE,"E12.6.0"),sQuery(id+"F0.wireOp",EDGE,"E12.6.1"),sQuery(id+"F0.wireOp",EDGE,"E12.6.2"),sQuery(id+"F0.wireOp",EDGE,"E12.6.3"),sQuery(id+"F0.wireOp",EDGE,"E12.6.4"),sQuery(id+"F0.wireOp",EDGE,"E12.6.5"),sQuery(id+"F0.wireOp",EDGE,"E12.6.6"),sQuery(id+"F0.wireOp",EDGE,"E12.6.7"),sQuery(id+"F0.wireOp",EDGE,"E12.6.8"),sQuery(id+"F0.wireOp",EDGE,"E12.6.9"),sQuery(id+"F0.wireOp",EDGE,"E12.7.0"),sQuery(id+"F0.wireOp",EDGE,"E12.7.1"),sQuery(id+"F0.wireOp",EDGE,"E12.7.2"),sQuery(id+"F0.wireOp",EDGE,"E12.7.3"),sQuery(id+"F0.wireOp",EDGE,"E12.7.4"),sQuery(id+"F0.wireOp",EDGE,"E12.7.5"),sQuery(id+"F0.wireOp",EDGE,"E12.7.6"),sQuery(id+"F0.wireOp",EDGE,"E12.7.7"),sQuery(id+"F0.wireOp",EDGE,"E12.7.8"),sQuery(id+"F0.wireOp",EDGE,"E12.7.9"),sQuery(id+"F0.wireOp",EDGE,"E12.8.0"),sQuery(id+"F0.wireOp",EDGE,"E12.8.1"),sQuery(id+"F0.wireOp",EDGE,"E12.8.2"),sQuery(id+"F0.wireOp",EDGE,"E12.8.3"),sQuery(id+"F0.wireOp",EDGE,"E12.8.4"),sQuery(id+"F0.wireOp",EDGE,"E12.8.5"),sQuery(id+"F0.wireOp",EDGE,"E12.8.6"),sQuery(id+"F0.wireOp",EDGE,"E12.8.7"),sQuery(id+"F0.wireOp",EDGE,"E12.8.8"),sQuery(id+"F0.wireOp",EDGE,"E12.8.9"),sQuery(id+"F0.wireOp",EDGE,"E12.9.0"),sQuery(id+"F0.wireOp",EDGE,"E12.9.1"),sQuery(id+"F0.wireOp",EDGE,"E12.9.2"),sQuery(id+"F0.wireOp",EDGE,"E12.9.3"),sQuery(id+"F0.wireOp",EDGE,"E12.9.4"),sQuery(id+"F0.wireOp",EDGE,"E12.9.5"),sQuery(id+"F0.wireOp",EDGE,"E12.9.6"),sQuery(id+"F0.wireOp",EDGE,"E12.9.7"),sQuery(id+"F0.wireOp",EDGE,"E12.9.8"),sQuery(id+"F0.wireOp",EDGE,"E12.9.9"),sQuery(id+"F0.wireOp",EDGE,"E12.10.0"),sQuery(id+"F0.wireOp",EDGE,"E12.10.1"),sQuery(id+"F0.wireOp",EDGE,"E12.10.2"),sQuery(id+"F0.wireOp",EDGE,"E12.10.3"),sQuery(id+"F0.wireOp",EDGE,"E12.10.4"),sQuery(id+"F0.wireOp",EDGE,"E12.10.5"),sQuery(id+"F0.wireOp",EDGE,"E12.10.6"),sQuery(id+"F0.wireOp",EDGE,"E12.10.7"),sQuery(id+"F0.wireOp",EDGE,"E12.10.8"),sQuery(id+"F0.wireOp",EDGE,"E12.10.9"),sQuery(id+"F0.wireOp",EDGE,"E12.11.0"),sQuery(id+"F0.wireOp",EDGE,"E12.11.1"),sQuery(id+"F0.wireOp",EDGE,"E12.11.2"),sQuery(id+"F0.wireOp",EDGE,"E12.11.3"),sQuery(id+"F0.wireOp",EDGE,"E12.11.4"),sQuery(id+"F0.wireOp",EDGE,"E12.11.5"),sQuery(id+"F0.wireOp",EDGE,"E12.11.6"),sQuery(id+"F0.wireOp",EDGE,"E12.11.7"),sQuery(id+"F0.wireOp",EDGE,"E12.11.8"),sQuery(id+"F0.wireOp",EDGE,"E12.11.9"),sQuery(id+"F0.wireOp",EDGE,"E12.12.0"),sQuery(id+"F0.wireOp",EDGE,"E12.12.1"),sQuery(id+"F0.wireOp",EDGE,"E12.12.2"),sQuery(id+"F0.wireOp",EDGE,"E12.12.3"),sQuery(id+"F0.wireOp",EDGE,"E12.12.4"),sQuery(id+"F0.wireOp",EDGE,"E12.12.5"),sQuery(id+"F0.wireOp",EDGE,"E12.12.6"),sQuery(id+"F0.wireOp",EDGE,"E12.12.7"),sQuery(id+"F0.wireOp",EDGE,"E12.12.8"),sQuery(id+"F0.wireOp",EDGE,"E12.12.9"),sQuery(id+"F0.wireOp",EDGE,"E12.13.0"),sQuery(id+"F0.wireOp",EDGE,"E12.13.1"),sQuery(id+"F0.wireOp",EDGE,"E12.13.2"),sQuery(id+"F0.wireOp",EDGE,"E12.13.3"),sQuery(id+"F0.wireOp",EDGE,"E12.13.4"),sQuery(id+"F0.wireOp",EDGE,"E12.13.5"),sQuery(id+"F0.wireOp",EDGE,"E12.13.6"),sQuery(id+"F0.wireOp",EDGE,"E12.13.7"),sQuery(id+"F0.wireOp",EDGE,"E12.13.8"),sQuery(id+"F0.wireOp",EDGE,"E12.13.9"),sQuery(id+"F0.wireOp",EDGE,"E12.14.0"),sQuery(id+"F0.wireOp",EDGE,"E12.14.1"),sQuery(id+"F0.wireOp",EDGE,"E12.14.2"),sQuery(id+"F0.wireOp",EDGE,"E12.14.3"),sQuery(id+"F0.wireOp",EDGE,"E12.14.4"),sQuery(id+"F0.wireOp",EDGE,"E12.14.5"),sQuery(id+"F0.wireOp",EDGE,"E12.14.6"),sQuery(id+"F0.wireOp",EDGE,"E12.14.7"),sQuery(id+"F0.wireOp",EDGE,"E12.14.8"),sQuery(id+"F0.wireOp",EDGE,"E12.14.9"),sQuery(id+"F0.wireOp",EDGE,"E12.15.0"),sQuery(id+"F0.wireOp",EDGE,"E12.15.1"),sQuery(id+"F0.wireOp",EDGE,"E12.15.2"),sQuery(id+"F0.wireOp",EDGE,"E12.15.3"),sQuery(id+"F0.wireOp",EDGE,"E12.15.4"),sQuery(id+"F0.wireOp",EDGE,"E12.15.5"),sQuery(id+"F0.wireOp",EDGE,"E12.15.6"),sQuery(id+"F0.wireOp",EDGE,"E12.15.7"),sQuery(id+"F0.wireOp",EDGE,"E12.15.8"),sQuery(id+"F0.wireOp",EDGE,"E12.15.9"),sQuery(id+"F0.wireOp",EDGE,"E12.16.0"),sQuery(id+"F0.wireOp",EDGE,"E12.16.1"),sQuery(id+"F0.wireOp",EDGE,"E12.16.2"),sQuery(id+"F0.wireOp",EDGE,"E12.16.3"),sQuery(id+"F0.wireOp",EDGE,"E12.16.4"),sQuery(id+"F0.wireOp",EDGE,"E12.16.5"),sQuery(id+"F0.wireOp",EDGE,"E12.16.6"),sQuery(id+"F0.wireOp",EDGE,"E12.16.7"),sQuery(id+"F0.wireOp",EDGE,"E12.16.8"),sQuery(id+"F0.wireOp",EDGE,"E12.16.9"),sQuery(id+"F0.wireOp",EDGE,"E12.17.0"),sQuery(id+"F0.wireOp",EDGE,"E12.17.1"),sQuery(id+"F0.wireOp",EDGE,"E12.17.2"),sQuery(id+"F0.wireOp",EDGE,"E12.17.3"),sQuery(id+"F0.wireOp",EDGE,"E12.17.4"),sQuery(id+"F0.wireOp",EDGE,"E12.17.5"),sQuery(id+"F0.wireOp",EDGE,"E12.17.6"),sQuery(id+"F0.wireOp",EDGE,"E12.17.7"),sQuery(id+"F0.wireOp",EDGE,"E12.17.8"),sQuery(id+"F0.wireOp",EDGE,"E12.17.9"),sQuery(id+"F0.wireOp",EDGE,"E12.18.0"),sQuery(id+"F0.wireOp",EDGE,"E12.18.1"),sQuery(id+"F0.wireOp",EDGE,"E12.18.2"),sQuery(id+"F0.wireOp",EDGE,"E12.18.3"),sQuery(id+"F0.wireOp",EDGE,"E12.18.4"),sQuery(id+"F0.wireOp",EDGE,"E12.18.5"),sQuery(id+"F0.wireOp",EDGE,"E12.18.6"),sQuery(id+"F0.wireOp",EDGE,"E12.18.7"),sQuery(id+"F0.wireOp",EDGE,"E12.18.8"),sQuery(id+"F0.wireOp",EDGE,"E12.18.9"),sQuery(id+"F0.wireOp",EDGE,"E12.19.0"),sQuery(id+"F0.wireOp",EDGE,"E12.19.1"),sQuery(id+"F0.wireOp",EDGE,"E12.19.2"),sQuery(id+"F0.wireOp",EDGE,"E12.19.3"),sQuery(id+"F0.wireOp",EDGE,"E12.19.4"),sQuery(id+"F0.wireOp",EDGE,"E12.19.5"),sQuery(id+"F0.wireOp",EDGE,"E12.19.6"),sQuery(id+"F0.wireOp",EDGE,"E12.19.7"),sQuery(id+"F0.wireOp",EDGE,"E12.19.8"),sQuery(id+"F0.wireOp",EDGE,"E12.19.9"),sQuery(id+"F0.wireOp",EDGE,"E12.20.0"),sQuery(id+"F0.wireOp",EDGE,"E12.20.1"),sQuery(id+"F0.wireOp",EDGE,"E12.20.2"),sQuery(id+"F0.wireOp",EDGE,"E12.20.3"),sQuery(id+"F0.wireOp",EDGE,"E12.20.4"),sQuery(id+"F0.wireOp",EDGE,"E12.20.5"),sQuery(id+"F0.wireOp",EDGE,"E12.20.6"),sQuery(id+"F0.wireOp",EDGE,"E12.20.7"),sQuery(id+"F0.wireOp",EDGE,"E12.20.8"),sQuery(id+"F0.wireOp",EDGE,"E12.20.9"),sQuery(id+"F0.wireOp",EDGE,"E12.21.0"),sQuery(id+"F0.wireOp",EDGE,"E12.21.1"),sQuery(id+"F0.wireOp",EDGE,"E12.21.2"),sQuery(id+"F0.wireOp",EDGE,"E12.21.3"),sQuery(id+"F0.wireOp",EDGE,"E12.21.4"),sQuery(id+"F0.wireOp",EDGE,"E12.21.5"),sQuery(id+"F0.wireOp",EDGE,"E12.21.6"),sQuery(id+"F0.wireOp",EDGE,"E12.21.7"),sQuery(id+"F0.wireOp",EDGE,"E12.21.8"),sQuery(id+"F0.wireOp",EDGE,"E12.21.9"),sQuery(id+"F0.wireOp",EDGE,"E12.22.0"),sQuery(id+"F0.wireOp",EDGE,"E12.22.1"),sQuery(id+"F0.wireOp",EDGE,"E12.22.2"),sQuery(id+"F0.wireOp",EDGE,"E12.22.3"),sQuery(id+"F0.wireOp",EDGE,"E12.22.4"),sQuery(id+"F0.wireOp",EDGE,"E12.22.5"),sQuery(id+"F0.wireOp",EDGE,"E12.22.6"),sQuery(id+"F0.wireOp",EDGE,"E12.22.7"),sQuery(id+"F0.wireOp",EDGE,"E12.22.8"),sQuery(id+"F0.wireOp",EDGE,"E12.22.9"),sQuery(id+"F0.wireOp",EDGE,"E12.23.0"),sQuery(id+"F0.wireOp",EDGE,"E12.23.1"),sQuery(id+"F0.wireOp",EDGE,"E12.23.2"),sQuery(id+"F0.wireOp",EDGE,"E12.23.3"),sQuery(id+"F0.wireOp",EDGE,"E12.23.4"),sQuery(id+"F0.wireOp",EDGE,"E12.23.5"),sQuery(id+"F0.wireOp",EDGE,"E12.23.6"),sQuery(id+"F0.wireOp",EDGE,"E12.23.7"),sQuery(id+"F0.wireOp",EDGE,"E12.23.8"),sQuery(id+"F0.wireOp",EDGE,"E12.23.9")])],"isStart":false});
            var sketch = newSketch(context, id + "F2", { "sketchPlane" : qUnion([Q0])});
            skCircle(sketch, "E13", {"center": v(0, 0) * mm, "radius": 3.81 * mm});
            skSolve(sketch);
        }
        {
            var Q0;
            Q0 = qSketchRegion(id + "F2", true);
            extrude(context, id + "F3", {"entities" : qUnion([Q0]), "operationType" : NewBodyOperationType.ADD, "depth" : 25.4 * mm});
        }
    });
